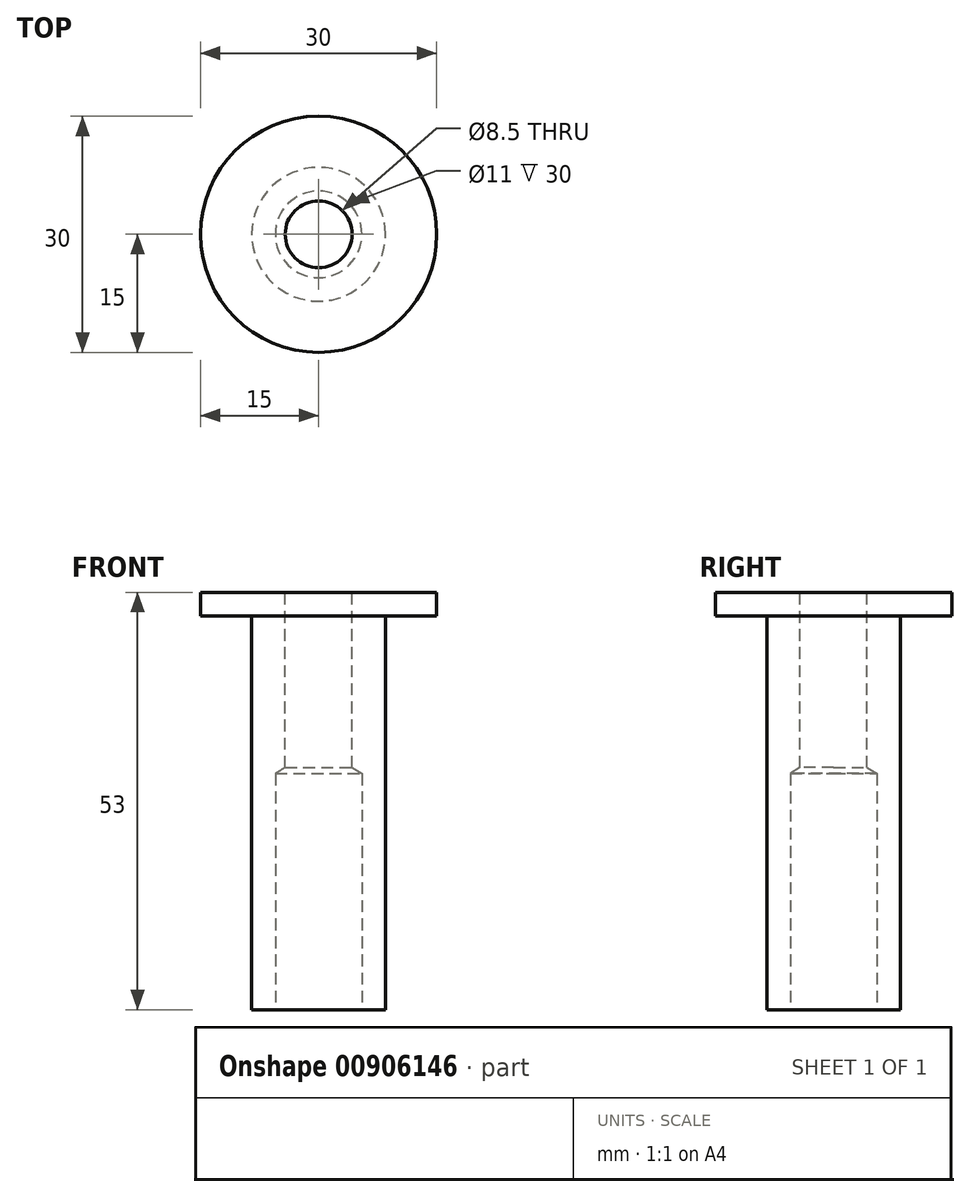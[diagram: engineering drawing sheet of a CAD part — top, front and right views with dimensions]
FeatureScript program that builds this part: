
annotation { "Feature Type Name" : "Feature", "Feature Type Description" : "" }
export const myFeature = defineFeature(function(context is Context, id is Id, definition is map)
    precondition{}
    {
        {
            var Q0;
            Q0=qCreatedBy(makeId("Front.planeOp"),FACE);
            var sketch = newSketch(context, id + "F0", { "sketchPlane" : qUnion([Q0])});
            skLineSegment(sketch, "E0", {"start": v(0, 0) * mm, "end": v(0, 53) * mm});
            skLineSegment(sketch, "E1", {"start": v(0, 53) * mm, "end": v(15, 53) * mm});
            skLineSegment(sketch, "E2", {"start": v(15, 53) * mm, "end": v(15, 50) * mm});
            skLineSegment(sketch, "E3", {"start": v(15, 50) * mm, "end": v(8.5, 50) * mm});
            skLineSegment(sketch, "E4", {"start": v(8.5, 50) * mm, "end": v(8.5, 0) * mm});
            skLineSegment(sketch, "E5", {"start": v(8.5, 0) * mm, "end": v(0, 0) * mm});
            skLineSegment(sketch, "E6", {"start": v(0, 0) * mm, "end": v(0, 71.61) * mm, "construction": true});
            skSolve(sketch);
        }
        {
            var Q0;
            Q0=qSketchRegion(id+"F0",true);
            var Q1;
            Q1=sQuery(id+"F0.wireOp",EDGE,"E6");
            revolve(context, id + "F1", {"surfaceOperationType" : NewSurfaceOperationType.NEW, "entities" : qUnion([Q0]), "axis" : qUnion([Q1]), "revolveType" : RevolveType.FULL});
        }
        {
            var Q0;
            Q0=makeQuery(id+"F1.opRevolve","SWEPT_FACE",FACE,{"disambiguationData":[OSD([sQuery(id+"F0.wireOp",EDGE,"E1")])]});
            var sketch = newSketch(context, id + "F2", { "sketchPlane" : qUnion([Q0])});
            skPoint(sketch, "E7", {"position": v(0, 0) * mm});
            skSolve(sketch);
        }
        {
            var Q0;
            Q0=sQuery(id+"F2.wireOp",VERTEX,"E7");
            var Q1;
            Q1=makeQuery(id+"F1.opRevolve","SWEPT_BODY",BODY,{"disambiguationData":[OSD([sQuery(id+"F0.wireOp",EDGE,"E0"),sQuery(id+"F0.wireOp",EDGE,"E1"),sQuery(id+"F0.wireOp",EDGE,"E2"),sQuery(id+"F0.wireOp",EDGE,"E3"),sQuery(id+"F0.wireOp",EDGE,"E4"),sQuery(id+"F0.wireOp",EDGE,"E5")])]});
            hole(context, id + "F3", {"style" : HoleStyle.SIMPLE, "endStyle" : HoleEndStyle.BLIND, "standardTappedOrClearance" : lookupTablePath({ "standard" : "ISO", "engagement" : "75%", "pitch" : "1.5 mm", "size" : "M10", "type" : "Tapped" }), "standardBlindInLast" : lookupTablePath({ "standard" : "ISO", "engagement" : "75%", "pitch" : "1.5 mm", "size" : "M10", "type" : "Tapped" }), "holeDiameter" : 8.5 * mm, "majorDiameter" : 10 * mm, "showTappedDepth" : true, "holeDepth" : 25 * mm, "isTappedThrough" : true, "tappedDepth" : 25 * mm, "tapClearance" : 0, "locations" : qUnion([Q0]), "scope" : qUnion([Q1])});
        }
        {
            var Q0;
            Q0=makeQuery(id+"F1.opRevolve","SWEPT_FACE",FACE,{"disambiguationData":[OSD([sQuery(id+"F0.wireOp",EDGE,"E5")])]});
            var sketch = newSketch(context, id + "F4", { "sketchPlane" : qUnion([Q0])});
            skPoint(sketch, "E8", {"position": v(0, 0) * mm});
            skSolve(sketch);
        }
        {
            var Q0;
            Q0=sQuery(id+"F4.wireOp",VERTEX,"E8");
            var Q1;
            Q1=makeQuery(id+"F1.opRevolve","SWEPT_BODY",BODY,{"disambiguationData":[OSD([sQuery(id+"F0.wireOp",EDGE,"E0"),sQuery(id+"F0.wireOp",EDGE,"E1"),sQuery(id+"F0.wireOp",EDGE,"E2"),sQuery(id+"F0.wireOp",EDGE,"E3"),sQuery(id+"F0.wireOp",EDGE,"E4"),sQuery(id+"F0.wireOp",EDGE,"E5")])]});
            hole(context, id + "F5", {"style" : HoleStyle.SIMPLE, "endStyle" : HoleEndStyle.BLIND, "holeDiameter" : 11 * mm, "majorDiameter" : 8 * mm, "holeDepth" : 30 * mm, "isTappedThrough" : true, "tappedDepth" : 16.25 * mm, "tapClearance" : 3, "locations" : qUnion([Q0]), "scope" : qUnion([Q1])});
        }
    });
